# Revit family: QF_BOURGEAT_Satellite4G_neutre_2-1_porte_pleine
name_source: partatom
category: Equipement spécialisé
revit_build: Autodesk Revit 2015 (Build: 20140606_1530(x64)
units: mm (PartAtom-declared; Revit-internal decimal feet)

## types (6) — shared parameters
Certification = NF hygiene alimentaire
Diametre_roue = 160 mm  [stored 0.524934 ft]
Fabricant = BOURGEAT
Hauteur_roue = 200 mm  [stored 0.656168 ft]
Largeur_porte = 706 mm  [stored 2.31627 ft]
Longueur hors tout = 791 mm
Longueur_poignees_laterales = 803 mm  [stored 2.63451 ft]
Materiau_Poignee_porte = B_Elastomère_TPE_S
Materiau_bac = B_Elastomère_TPE_S
Materiau_bandage = B_Elastomère_TPE_S
Materiau_porte = Acier inoxydable, brossé
Materiau_vitre = Verre, vitrage transparent, trempé
Nature isolant = Mousse sans PU
Pos_V_IHM = 100 mm  [stored 0.328084 ft]
Profondeur hors tout = 959 mm  [stored 3.14633 ft]
Spécification du Fabricant = Satellite 4G
URL catalogue = http://www.bourgeat.fr

## per-type parameters (varying)
| type | Charge max | Hauteur hors tout | Hauteur_poignee_porte_sol | Hauteur_poignees_laterales | Hauteur_porte | Modèle | Poids net à vide | Poignee_droite | Poignee_gauche |
| GN30_neutre_porte_inox_tirant_droit | 250.00 kg | 1521 mm  [stored 4.99016 ft] | 515 mm  [stored 1.68963 ft] | 908 mm  [stored 2.979 ft] | 1274 mm  [stored 4.17979 ft] | 840130 + 844000 | 120.00 kg | Oui | Non |
| GN40_neutre_porte_inox_tirant_droit | 300.00 kg | 1876 mm | 767 mm  [stored 2.5164 ft] | 906 mm  [stored 2.97244 ft] | 1629 mm  [stored 5.34449 ft] | 8400140 + 844000 | 140.00 kg | Oui | Non |
| GN20_neutre_porte_inox_tirant_droit | 200.00 kg | 1166 mm | 480 mm  [stored 1.5748 ft] | 806 mm  [stored 2.64436 ft] | 919 mm | 840120 + 844000 | 100.00 kg | Oui | Non |
| GN20_neutre_porte_inox_tirant_gauche | 200.00 kg | 1166 mm | 480 mm  [stored 1.5748 ft] | 806 mm  [stored 2.64436 ft] | 919 mm | 840120 | 100.00 kg | Non | Oui |
| GN30_neutre_porte_inox_tirant_gauche | 300.00 kg | 1521 mm  [stored 4.99016 ft] | 515 mm  [stored 1.68963 ft] | 908 mm  [stored 2.979 ft] | 1274 mm  [stored 4.17979 ft] | 840130 | 140.00 kg | Non | Oui |
| GN40_neutre_porte_inox_tirant_gauche | 300.00 kg | 1876 mm | 767 mm  [stored 2.5164 ft] | 906 mm  [stored 2.97244 ft] | 1629 mm  [stored 5.34449 ft] | 8400140 | 140.00 kg | Oui | Non |

note: [stored X ft] marks values corroborated as IEEE doubles in the binary element streams (Revit-internal decimal feet)
